# Revit family: IS_Ceraline_BC268_BIM_NL
name_source: partatom
category: Plumbing Fixtures
units: mm (PartAtom-declared; Revit-internal decimal feet)

## family parameters
Always vertical = No
Cut with Voids When Loaded = No
OmniClass Number = 23.45.55.17
OmniClass Title = Mixing Faucets
Part Type = Normal
Room Calculation Point = No
Round Connector Dimension = Use Diameter
Shared = No
Work Plane-Based = No

## types (2) — shared parameters
Accesoires = https://www.idealstandard.nl
Afmetingen = 146 x 135 x 50 mm
AfstandsEenheid = Millimeter
Artikelreferentie = CERALINE WASCHTISCHMISCHER RIM-MONTAGE 5L PRO MINUTE
Auteur = Ideal Standard
BIMObjectName = Washbasin manual water supply sets_Ceraline_BC268_Ideal Standard
BIMobject category = Sanitary
BIMobject category code = Sanitary Taps & Mixer
BIMobject main category = Sanitary
BIMobject main category code = sanitary
BOSUseNativeGeometries = 1
Bedieningkraan = Handbuch
Bedieningkraanwerk = einzelne Ebene
Beschrijvinggarantie = Herstellergarantie
BimObjectNaam = Washbasin manual water supply sets_Ceraline_BC268_Ideal Standard
Brand url = http://www.idealstandard.nl
Breedte = 50.000001
Date of publishing = 20/05/2019
Diepte = 135 mm
DikteMateriaal = Messing
Doorstromingscoëfficiënt = 5L/min
Douchebak = No
DuurEenheid = Jaren
Edition number = 1
Features = CERALINE BSN MXR RMTD CHR 5LPM    MENA
Functiekraanwerk = Einhebelgriff
Garantieunits = Jaren
GemaaktOp = 22/07/2021
Hoogte = 146.400000000044
Hulp = https://www.idealstandard.nl
IFC Classification = Sanitary Terminal
IfcExportAs = Sanitary Terminal
IfcExportType = FAUCET
Installatieinstructies = https://www.idealstandard.nl
Installation instructions = https://www.idealstandard.nl
Lengte = 135 mm
Manufacturer name = Ideal Standard
Masterformat 2014 Code = 41 14 33
Masterformat 2014 Description = Mixer
Materiaal = Messing
Merk = Ideal Standard
ModelReference = CERALINE BSN MXR RMTD CHR 5LPM    MENA
Montageinstuctie = https://www.idealstandard.nl
NBS Reference Code = 45-35-70/371
NBS Reference Description = Washbasin manual water supply sets
Name = IS_IdealStandard_Washbasinmanualwatersupplysets_Ceraline_BC268
Nettogewicht = 0.89
NominalHeight = 146 mm
NominalLength = 135 mm
NominalWidth = 50 mm
Normen = IS_IdealStandard_Washbasinmanualwatersupplysets_Ceraline_BC268
OmniClass Code = 23-31 11 00
OmniClass Description = Faucets
OppervlakteEenheid = Millimeter
Product Guid = 4523e16c-b03f-4949-aa4a-f86a855cf52a
Product certification = https://www.idealstandard.nl
Product data url = https://bimobject.com
Product family = Ceraline
Product group = Washbasin manual water supply sets
Product name = CERALINE BSN MXR RMTD CHR 5LPM    MENA
Product url = https://www.idealstandard.nl
ProductSoort = Armaturen Mixer
Productinformatie = https://www.idealstandard.nl
QR code = http://bimobject.com
Referentie = CERALINE BSN MXR RMTD CHR 5LPM    MENA
Revisie = 1
Size = 146 x 135 x 50 mm
Technical description = https://www.idealstandard.nl
Telefoonnummer = 077 355 08 08
Testdruk = 10 Bar
Typeconnectie = Installation
URL = https://www.idealstandard.nl
Uniclass 1.4 Code = L725111
Uniclass 1.4 Description = Mixers taps
Uniclass 2015 Code = Pr_40_20_87_96
Uniclass 2015 Name = Washbasin manual water supply sets
Uniclass2015Beschrijving = Washbasin manual water supply sets
Uniclass2015Referentie = Pr_40_20_87_96
Uniclass2015Version = v1.22
Urlproducent = https://www.idealstandard.nl
ValutaEenheid = Euro
Versie = 1
Volumeunits = Liter
Vorm = zylindrisch
WarrantyDescription = Manufacturers Warranty
WarrantyDurationParts = 5
WarrantyDurationUnit = year
Wisselstukken = https://www.idealstandard.nl
Youtube clip = https://www.youtube.com
zero-valued in all types: BrutoGewicht, Cost, Overloop, Vervangingskosten

## per-type parameters (varying)
| type | Afwerking | Artikelnummer | Artikelomschrijving | BarCode | Barcode | Description | Eigenschappen | Finish | GTIN code | Kleur | Model | ModelNumber | Product SKU |
| BC268AA - CERALINE BASIN MIXER RIM-MOUNTED 5L PER MINUTE - CHROME | chrom | BC268AA | CERALINE WASCHTISCHMISCHER RIM-MONTAGE 5L PRO MINUTE - CHROM | 3800861065180 | 3800861065180 | CERALINE BASIN MIXER RIM-MOUNTED 5L PER MINUTE - CHROME | WASCHTISCHMISCHER RIM-MONTAGE 5L PRO MINUTE - CHROM | chrom | https://3800861065180 | chrom | BC268AA | BC268AA | BC268AA |
| BC268XG - CERALINE BASIN MIXER RIM-MOUNTED 5L PER MINUTE - SILK BLACK | seide schwarz | BC268XG | CERALINE WASCHTISCHMISCHER RIM-MONTAGE 5L PRO MINUTE - SEIDE SCHWARZ | 3800861101680 | 3800861101680 | CERALINE BASIN MIXER RIM-MOUNTED 5L PER MINUTE - SILK BLACK | WASCHTISCHMISCHER RIM-MONTAGE 5L PRO MINUTE - SEIDE SCHWARZ | seide schwarz | https://3800861101680 | seide schwarz | BC268XG | BC268XG | BC268XG |

## geometry (parser evidence)
native form markers: Sweep x3
no freeform markers — native parametric forms only
